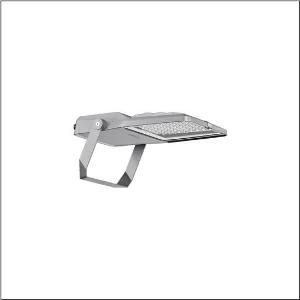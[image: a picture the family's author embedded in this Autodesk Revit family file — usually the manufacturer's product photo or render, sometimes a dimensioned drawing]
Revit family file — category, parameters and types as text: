
# Revit family: floodlight_fl_21_iq_mini___rs12_5xa7772d5b1a_d30b
name_source: partatom
category: Lighting Fixtures
units: mm (PartAtom-declared; Revit-internal decimal feet)

## family parameters
Cut with Voids When Loaded = No
Host = Face
Light Source = No
Part Type = Normal
Room Calculation Point = No
Round Connector Dimension = Use Diameter
Shared = No

## types (1)
- --- (1 x LED, 16820 lm, 143 W, 4000K)
    Apparent Load = 143 VA
    CIE Flux Codes = 79 92 99 100 100
    Color Rendering = 80
    Color Temperature = 4000K
    Default Elevation = 1800 mm
    Description = Floodlight FL 21 iQ mini, floodlight, primary light control with lens, of PMMA, primary optical cover: protective disc, of toughened safety glass, transparent, light distribution: RS12, light emission: direct distribution, installation type: surface-mounted, LED, High Power LED, rated luminous flux: 16.820lm, luminous efficacy: 118lm/W, light colour: 840, colour temperature: 4000K, control: Street-Remote, Auto-Match, Temp-Guard, Night-Set, Smart-Wire, Desk-Remote (wireless, voltage-free reading and setting of iQ features in the workshop via application-optimized NFC function/RFID function), optimised constant luminous flux control (CLO 2.0), with terminal, 6-pole, mains connection: 220..240V, AC, 50/60Hz, start of lifetime: 143W, end of service life: 152W, reduction: 61W, luminaire housing, of diecast aluminium, powder-coated, Siteco® metallic grey (DB 702S), corrosivity category C5 mid according to DIN EN ISO 12944, sealing non-destructively replaceable, mounting bracket, of steel, galvanised, powder-coated, Siteco® metallic grey (DB 702S), protection rating (complete): IP66, insulation class (complete): insulation class II (safety insulation), certification: CE, ENEC, VDE, protection symbol: D, impact resistance: IK08, permissible operating ambient temperature: -40..+40°C, permissible operating ambient temperature for outdoor applications: -40..+50°C, standard: DIN EN 12944, LABS conformity tested according to VDMA 24364:2018-05, packaging unit: 1 piece

Light Distribution: RS12
    Height = 70 mm
    Lamp = 1 x LED
    Lamp Light Flux = 16820 lm
    Lamp Power = 143 W
    Lamp count = 1
    Length = 485 mm
    Luminous efficacy = 118 lm/W
    Manufacturer = Siteco
    ModVariant = No
    Model = 5XA7772D5B1A
    Number of Poles = 1
    OnlyDefault = Yes
    Power Factor = 1
    Product Name = Floodlight FL 21 iQ mini | RS12
    Product group = floodlight | pylon annexe
    ProductGroupID = 6200
    Protection Class = Protection class II
    Protection Degree = IP 66
    RLX_Detail_Level = 1
    RLX_Emergency_Light_Flux = 0 lm
    RLX_Emergency_Type = 0
    RLX_Emergency_Type_DB = No
    RlxData = <blob elided: 91129 chars, md5=06820da6>
    Socket = socket
    Standby Power = 0 W
    System Light Flux = 16820 lm
    System Power = 143 W
    Type Comments = factory setting: luminous flux: 100 % | dim-lin: 254 | 730 mA
    Type Image = l_1006845.jpg
    URL = http://relux.com
    VarID = @adj_099577
    Voltage = 0 V
    Weight = 0.00 kg
    Width = 337 mm

## geometry (parser evidence)
native form markers: Blend x4, Sweep x13
no freeform markers — native parametric forms only
